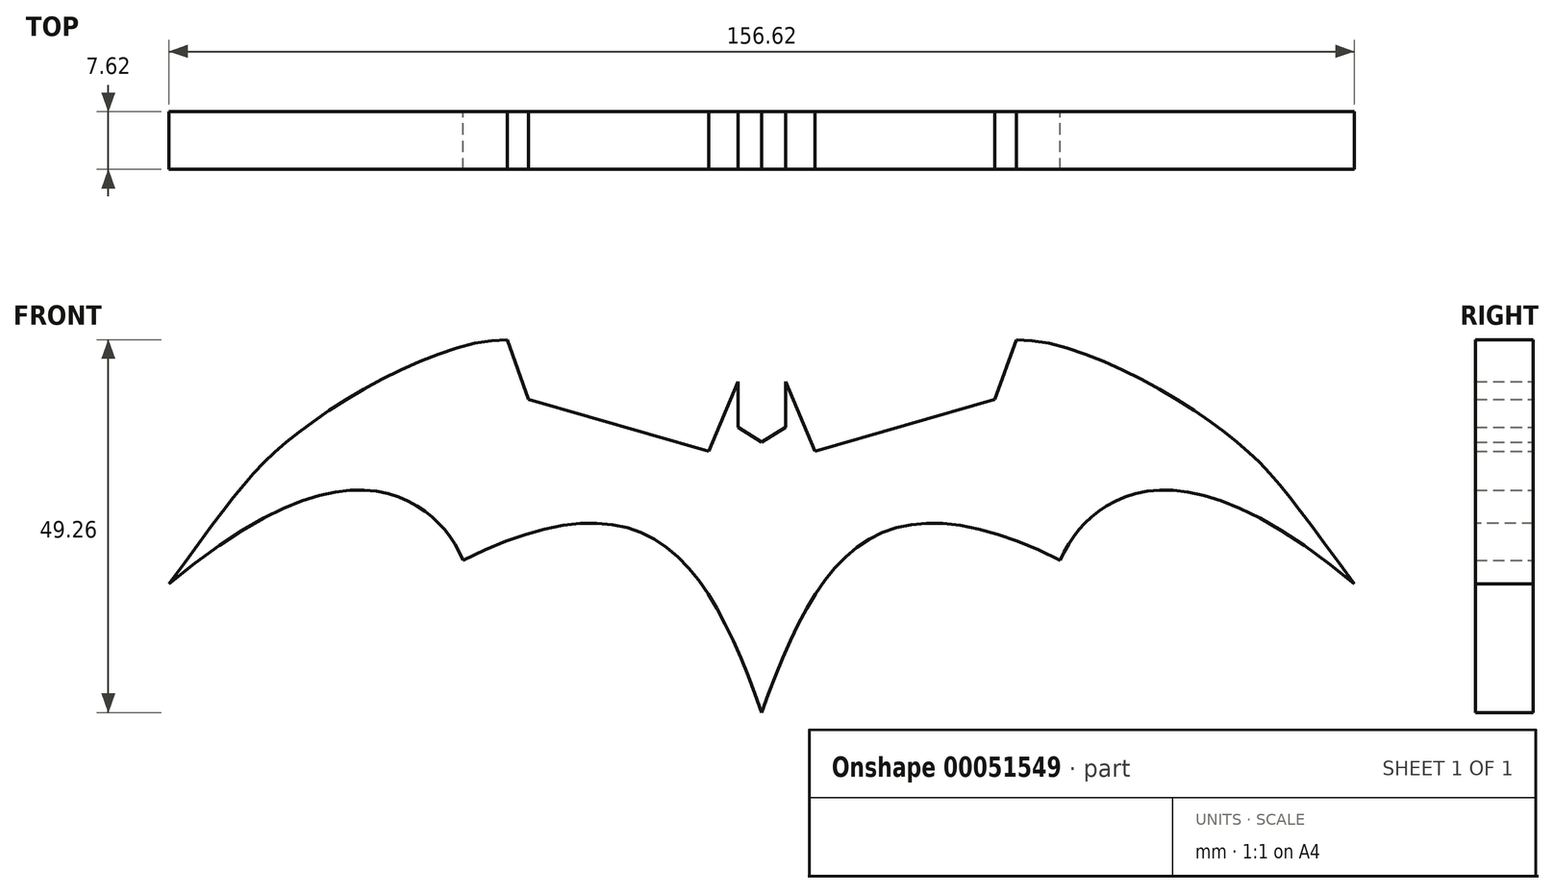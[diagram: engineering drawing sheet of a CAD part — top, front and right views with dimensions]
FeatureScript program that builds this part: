
annotation { "Feature Type Name" : "Feature", "Feature Type Description" : "" }
export const myFeature = defineFeature(function(context is Context, id is Id, definition is map)
    precondition{}
    {
        {
            var Q0;
            Q0=qCreatedBy(makeId("Front.planeOp"),FACE);
            var sketch = newSketch(context, id + "F0", { "sketchPlane" : qUnion([Q0])});
            skLineSegment(sketch, "E0", {"start": v(0, 0) * mm, "end": v(0, 35.74) * mm});
            skLineSegment(sketch, "E1", {"start": v(0, 35.74) * mm, "end": v(3.14, 37.7) * mm});
            skLineSegment(sketch, "E2", {"start": v(3.14, 37.7) * mm, "end": v(3.14, 43.7) * mm});
            skLineSegment(sketch, "E3", {"start": v(3.14, 43.7) * mm, "end": v(7.02, 34.5) * mm});
            skLineSegment(sketch, "E4", {"start": v(7.02, 34.5) * mm, "end": v(30.8, 41.36) * mm});
            skLineSegment(sketch, "E5", {"start": v(30.8, 41.36) * mm, "end": v(33.62, 49.26) * mm});
            skFitSpline(sketch, "E6", {"points": [v(33.62, 49.26) * mm, v(60.68, 37.41) * mm, v(78.3, 17) * mm], "startDerivative": vector(45.9, 0.7) * mm, "endDerivative": vector(51.14, -68.63) * mm});
            skFitSpline(sketch, "E7", {"points": [v(0, 0) * mm, v(13.37, 22.39) * mm, v(39.43, 20.09) * mm], "startDerivative": vector(20.43, 57.16) * mm, "endDerivative": vector(67.5, -34.6) * mm});
            skFitSpline(sketch, "E8", {"points": [v(39.43, 20.09) * mm, v(45.37, 27.18) * mm, v(78.3, 17) * mm], "startDerivative": vector(11.74, 26.13) * mm, "endDerivative": vector(81.37, -67.95) * mm});
            skLineSegment(sketch, "E9.MirrorCS", {"start": v(-7.02, 34.5) * mm, "end": v(-30.8, 41.36) * mm});
            skLineSegment(sketch, "E10.MirrorCS", {"start": v(0, 35.74) * mm, "end": v(-3.14, 37.7) * mm});
            skLineSegment(sketch, "E11.MirrorCS", {"start": v(-3.14, 37.7) * mm, "end": v(-3.14, 43.7) * mm});
            skLineSegment(sketch, "E12.MirrorCS", {"start": v(-3.14, 43.7) * mm, "end": v(-7.02, 34.5) * mm});
            skFitSpline(sketch, "E13.MirrorCS", {"points": [v(0, 0) * mm, v(-13.37, 22.39) * mm, v(-39.43, 20.09) * mm], "startDerivative": vector(-20.43, 57.16) * mm, "endDerivative": vector(-67.5, -34.6) * mm});
            skFitSpline(sketch, "E14.MirrorCS", {"points": [v(-39.43, 20.09) * mm, v(-45.37, 27.18) * mm, v(-78.3, 17) * mm], "startDerivative": vector(-11.74, 26.13) * mm, "endDerivative": vector(-81.37, -67.95) * mm});
            skFitSpline(sketch, "E15.MirrorCS", {"points": [v(-33.62, 49.26) * mm, v(-60.68, 37.41) * mm, v(-78.3, 17) * mm], "startDerivative": vector(-45.9, 0.7) * mm, "endDerivative": vector(-51.14, -68.63) * mm});
            skLineSegment(sketch, "E16.MirrorCS", {"start": v(-30.8, 41.36) * mm, "end": v(-33.62, 49.26) * mm});
            skSolve(sketch);
        }
        {
            var Q0;
            Q0=makeQuery(id+"F0.imprint","IMPRINT",FACE,{"disambiguationData":[TD([[makeQuery(id+"F0.imprint","IMPRINT",EDGE,{"derivedFrom":sQuery(id+"F0.wireOp",EDGE,"E0")}),1.0]])]});
            var Q1;
            Q1=makeQuery(id+"F0.imprint","IMPRINT",FACE,{"disambiguationData":[TD([[makeQuery(id+"F0.imprint","IMPRINT",EDGE,{"derivedFrom":sQuery(id+"F0.wireOp",EDGE,"E0")}),-1.0]])]});
            extrude(context, id + "F1", {"entities" : qUnion([Q0, Q1]), "depth" : 7.62 * mm});
        }
    });
